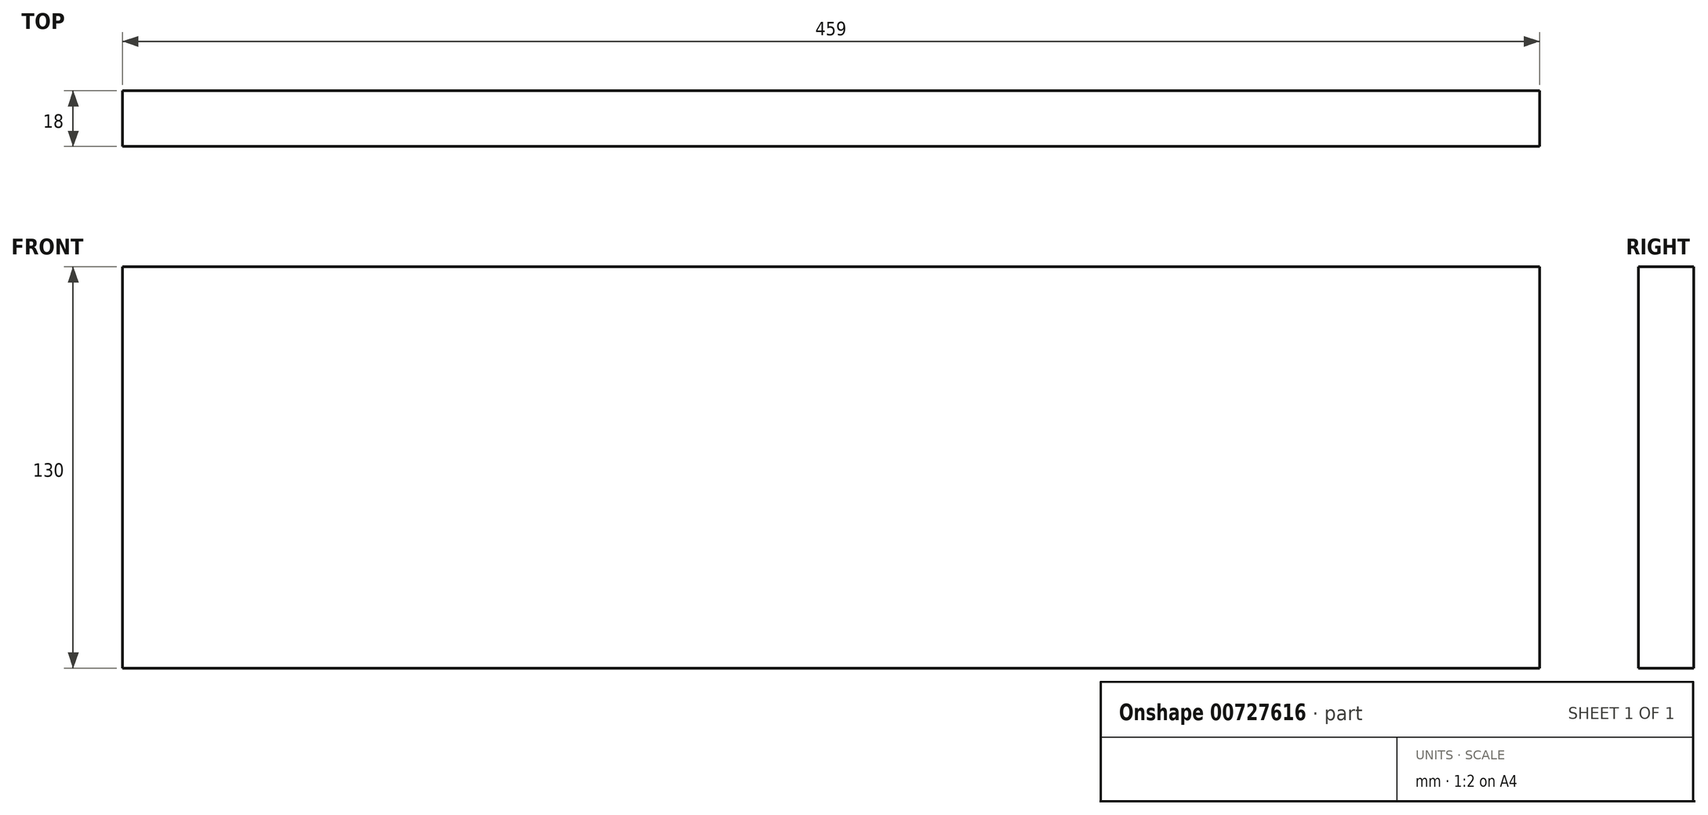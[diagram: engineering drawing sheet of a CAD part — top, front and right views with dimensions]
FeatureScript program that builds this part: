
annotation { "Feature Type Name" : "Feature", "Feature Type Description" : "" }
export const myFeature = defineFeature(function(context is Context, id is Id, definition is map)
    precondition{}
    {
        {
            var Q0;
            Q0=qCreatedBy(makeId("Front.planeOp"),FACE);
            var sketch = newSketch(context, id + "F0", { "sketchPlane" : qUnion([Q0])});
            skLineSegment(sketch, "E0.bottom", {"start": v(-229.5, 65) * mm, "end": v(229.5, 65) * mm});
            skLineSegment(sketch, "E0.top", {"start": v(-229.5, -65) * mm, "end": v(229.5, -65) * mm});
            skLineSegment(sketch, "E0.left", {"start": v(-229.5, 65) * mm, "end": v(-229.5, -65) * mm});
            skLineSegment(sketch, "E0.right", {"start": v(229.5, 65) * mm, "end": v(229.5, -65) * mm});
            skLineSegment(sketch, "E1", {"start": v(-229.5, 65) * mm, "end": v(229.5, -65) * mm, "construction": true});
            skSolve(sketch);
        }
        {
            var Q0;
            Q0 = qSketchRegion(id + "F0", true);
            extrude(context, id + "F1", {"entities" : qUnion([Q0]), "depth" : 18 * mm, "offsetDistance" : 25 * mm});
        }
    });
